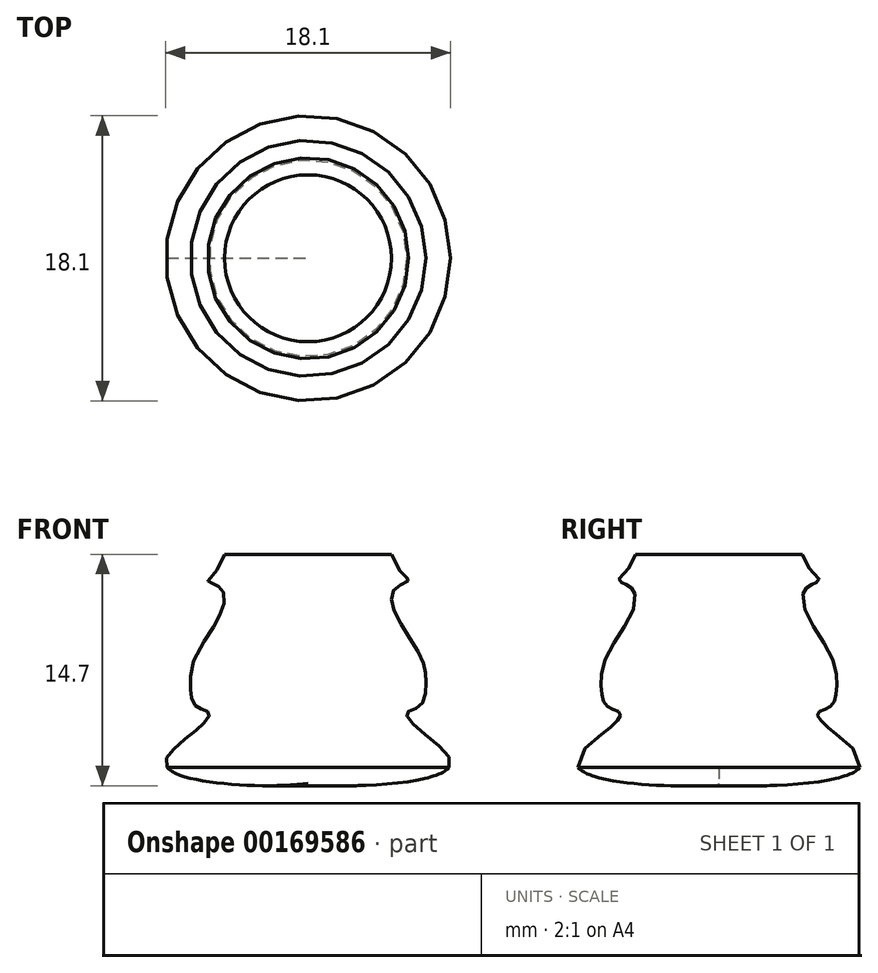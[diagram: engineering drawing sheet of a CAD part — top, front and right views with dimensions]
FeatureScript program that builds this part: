
annotation { "Feature Type Name" : "Feature", "Feature Type Description" : "" }
export const myFeature = defineFeature(function(context is Context, id is Id, definition is map)
    precondition{}
    {
        {
            var Q0;
            Q0=qCreatedBy(makeId("Front.planeOp"),FACE);
            var sketch = newSketch(context, id + "F0", { "sketchPlane" : qUnion([Q0])});
            skLineSegment(sketch, "E0.left", {"start": v(0, 42.86) * mm, "end": v(0, 38.2) * mm});
            skPoint(sketch, "E1.orphan", {"position": v(0, 46.2) * mm});
            skFitSpline(sketch, "E2", {"points": [v(-5, 38.2) * mm, v(-5, 36.1) * mm, v(-4.18, 35.16) * mm, v(-5.79, 26.78) * mm, v(-6.38, 26.1) * mm, v(-5.54, 25.6) * mm, v(-5.45, 24.24) * mm, v(-7.23, 21.1) * mm, v(-7.48, 19.59) * mm, v(-7.14, 18.15) * mm, v(-6.3, 17.73) * mm, v(-6.97, 16.71) * mm, v(-9, 14.3) * mm, v(0, 13.22) * mm], "startDerivative": vector(-4, -17.38) * mm, "endDerivative": vector(48.53, 7.54) * mm});
            skLineSegment(sketch, "E3", {"start": v(-8.96, 14.24) * mm, "end": v(0, 14.2) * mm});
            skLineSegment(sketch, "E4", {"start": v(0, 26.52) * mm, "end": v(0, 13.22) * mm});
            skPoint(sketch, "E5.orphan", {"position": v(216.1, 13.22) * mm});
            skLineSegment(sketch, "E6", {"start": v(0, 26.52) * mm, "end": v(0, 27.77) * mm});
            skLineSegment(sketch, "E7", {"start": v(-5.3, 27.77) * mm, "end": v(0, 27.77) * mm});
            skPoint(sketch, "E0.bottom.end.orphan", {"position": v(-5, 46.2) * mm});
            skSolve(sketch);
        }
        {
            var Q0;
            Q0=qCreatedBy(makeId("Front.planeOp"),FACE);
            var sketch = newSketch(context, id + "F1", { "sketchPlane" : qUnion([Q0])});
            skLineSegment(sketch, "E8", {"start": v(0, 42.86) * mm, "end": v(0, 13.5) * mm});
            skSolve(sketch);
        }
        {
            var Q0;
            Q0=qSketchRegion(id+"F0",true);
            var Q1;
            Q1=sQuery(id+"F1.wireOp",EDGE,"E8");
            revolve(context, id + "F2", {"entities" : qUnion([Q0]), "axis" : qUnion([Q1]), "revolveType" : RevolveType.FULL});
        }
    });
